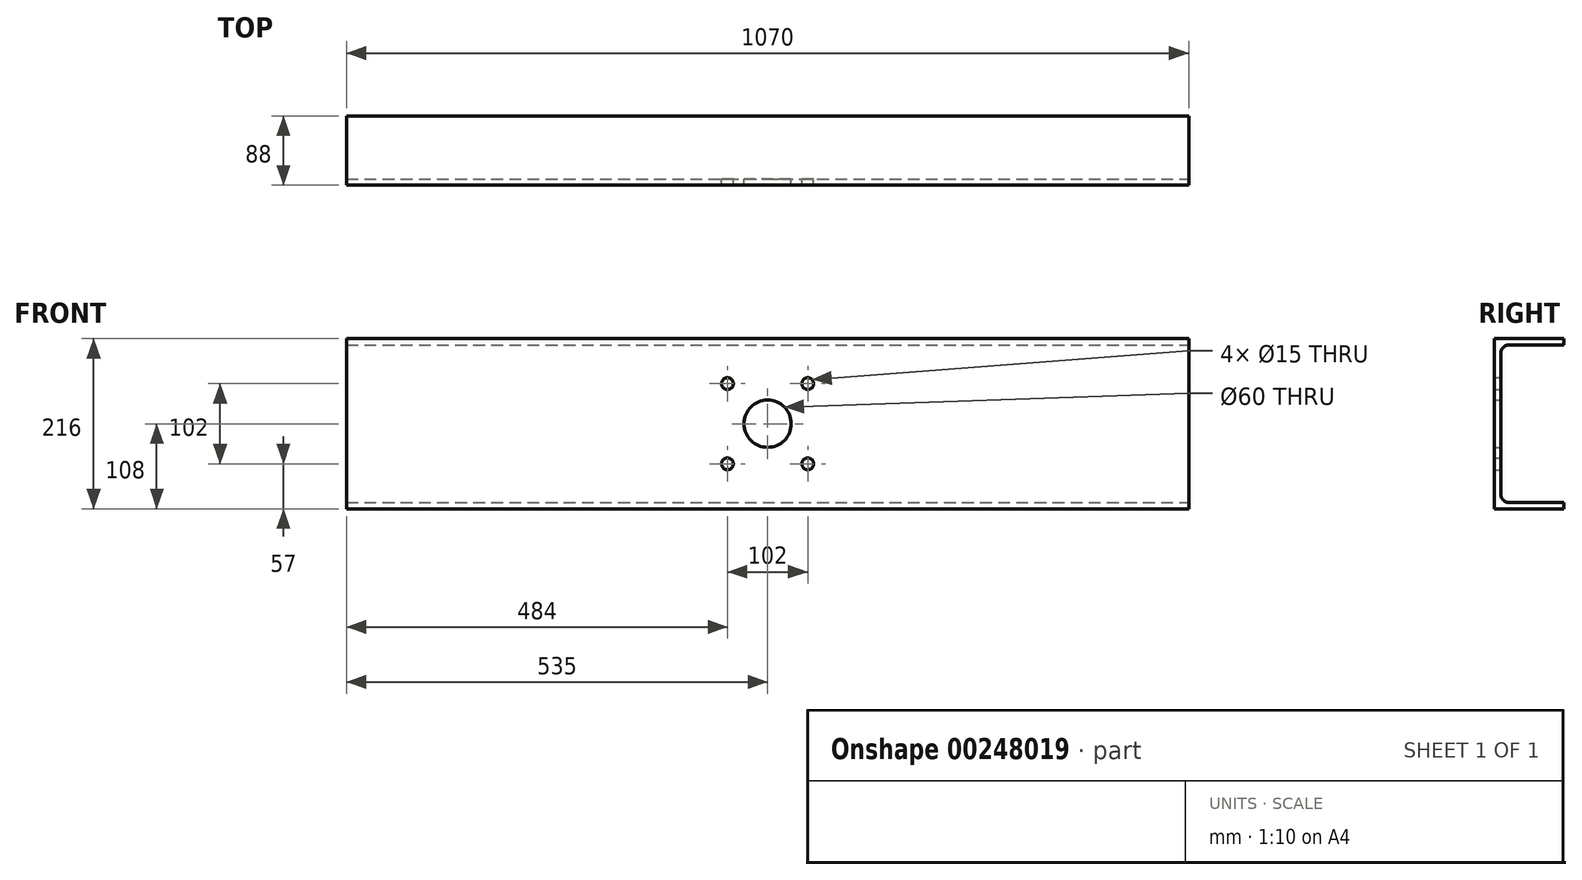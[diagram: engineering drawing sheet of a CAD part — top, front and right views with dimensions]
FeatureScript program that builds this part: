
annotation { "Feature Type Name" : "Feature", "Feature Type Description" : "" }
export const myFeature = defineFeature(function(context is Context, id is Id, definition is map)
    precondition{}
    {
        {
            var Q0;
            Q0=qCreatedBy(makeId("Front.planeOp"),FACE);
            var sketch = newSketch(context, id + "F0", { "sketchPlane" : qUnion([Q0])});
            skPoint(sketch, "E0.middle", {"position": v(0, 0) * mm});
            skLineSegment(sketch, "E1.bottom", {"start": v(-535, -100) * mm, "end": v(535, -100) * mm});
            skLineSegment(sketch, "E1.top", {"start": v(-535, 100) * mm, "end": v(535, 100) * mm});
            skLineSegment(sketch, "E1.left", {"start": v(-535, -100) * mm, "end": v(-535, 100) * mm});
            skLineSegment(sketch, "E1.right", {"start": v(535, -100) * mm, "end": v(535, 100) * mm});
            skPoint(sketch, "E2", {"position": v(-51, 51) * mm});
            skPoint(sketch, "E3", {"position": v(51, 51) * mm});
            skPoint(sketch, "E4", {"position": v(51, -51) * mm});
            skPoint(sketch, "E5", {"position": v(-51, -51) * mm});
            skSolve(sketch);
        }
        {
            var Q0;
            Q0=makeQuery(id+"F0.imprint","IMPRINT",FACE,{"disambiguationData":[TD([[makeQuery(id+"F0.imprint","IMPRINT",EDGE,{"derivedFrom":sQuery(id+"F0.wireOp",EDGE,"E1.bottom")}),1.0]])]});
            extrude(context, id + "F1", {"entities" : qUnion([Q0]), "oppositeDirection" : true, "depth" : 80 * mm});
        }
        {
            var Q0;
            Q0=makeQuery(id+"F1.opExtrude","CAP_FACE",FACE,{"disambiguationData":[OSD([sQuery(id+"F0.wireOp",EDGE,"E1.bottom"),sQuery(id+"F0.wireOp",EDGE,"E1.top"),sQuery(id+"F0.wireOp",EDGE,"E1.left"),sQuery(id+"F0.wireOp",EDGE,"E1.right")])],"isStart":false});
            var Q1;
            Q1=makeQuery(id+"F1.opExtrude","SWEPT_FACE",FACE,{"disambiguationData":[OSD([sQuery(id+"F0.wireOp",EDGE,"E1.right")])]});
            var Q2;
            Q2=makeQuery(id+"F1.opExtrude","SWEPT_FACE",FACE,{"disambiguationData":[OSD([sQuery(id+"F0.wireOp",EDGE,"E1.left")])]});
            shell(context, id + "F2", {"entities" : qUnion([Q0, Q1, Q2]), "thickness" : 8 * mm, "oppositeDirection" : true});
        }
        {
            var Q0;
            {var subQ0=sQuery(id+"F0.wireOp",EDGE,"E1.top");Q0=makeQuery(id+"F2.opShell","OFFSET_EDGE",EDGE,{"disambiguationData":[OSD([subQ0]),TDD([makeQuery(id+"F1.opExtrude","CAP_EDGE",EDGE,{"disambiguationData":[OSD([subQ0])],"isStart":true})])]});}
            var Q1;
            {var subQ0=sQuery(id+"F0.wireOp",EDGE,"E1.bottom");Q1=makeQuery(id+"F2.opShell","OFFSET_EDGE",EDGE,{"disambiguationData":[OSD([subQ0]),TDD([makeQuery(id+"F1.opExtrude","CAP_EDGE",EDGE,{"disambiguationData":[OSD([subQ0])],"isStart":true})])]});}
            fillet(context, id + "F3", {"entities" : qUnion([Q0, Q1]), "radius" : 10 * mm, "tangentPropagation" : true, "allowEdgeOverflow" : false});
        }
        {
            var Q0;
            Q0=sQuery(id+"F0.wireOp",VERTEX,"E0.middle");
            var Q1;
            Q1=makeQuery(id+"F1.opExtrude","SWEPT_BODY",BODY,{"disambiguationData":[OSD([sQuery(id+"F0.wireOp",EDGE,"E1.bottom"),sQuery(id+"F0.wireOp",EDGE,"E1.top"),sQuery(id+"F0.wireOp",EDGE,"E1.left"),sQuery(id+"F0.wireOp",EDGE,"E1.right")])]});
            hole(context, id + "F4", {"style" : HoleStyle.SIMPLE, "endStyle" : HoleEndStyle.THROUGH, "oppositeDirection" : true, "holeDiameter" : 60 * mm, "tappedDepth" : 12 * mm, "tapClearance" : 3, "locations" : qUnion([Q0]), "scope" : qUnion([Q1])});
        }
        {
            var Q0;
            Q0=sQuery(id+"F0.wireOp",VERTEX,"E2");
            var Q1;
            Q1=sQuery(id+"F0.wireOp",VERTEX,"E3");
            var Q2;
            Q2=sQuery(id+"F0.wireOp",VERTEX,"E4");
            var Q3;
            Q3=sQuery(id+"F0.wireOp",VERTEX,"E5");
            var Q4;
            Q4=makeQuery(id+"F1.opExtrude","SWEPT_BODY",BODY,{"disambiguationData":[OSD([sQuery(id+"F0.wireOp",EDGE,"E1.bottom"),sQuery(id+"F0.wireOp",EDGE,"E1.top"),sQuery(id+"F0.wireOp",EDGE,"E1.left"),sQuery(id+"F0.wireOp",EDGE,"E1.right")])]});
            hole(context, id + "F5", {"style" : HoleStyle.SIMPLE, "endStyle" : HoleEndStyle.THROUGH, "oppositeDirection" : true, "standardTappedOrClearance" : lookupTablePath({ "standard" : "ISO", "size" : "15", "type" : "Drilled" }), "standardBlindInLast" : lookupTablePath({ "standard" : "ISO", "size" : "15", "type" : "Drilled" }), "holeDiameter" : 15 * mm, "tappedDepth" : 12 * mm, "tapClearance" : 3, "locations" : qUnion([Q0, Q1, Q2, Q3]), "scope" : qUnion([Q4])});
        }
    });
